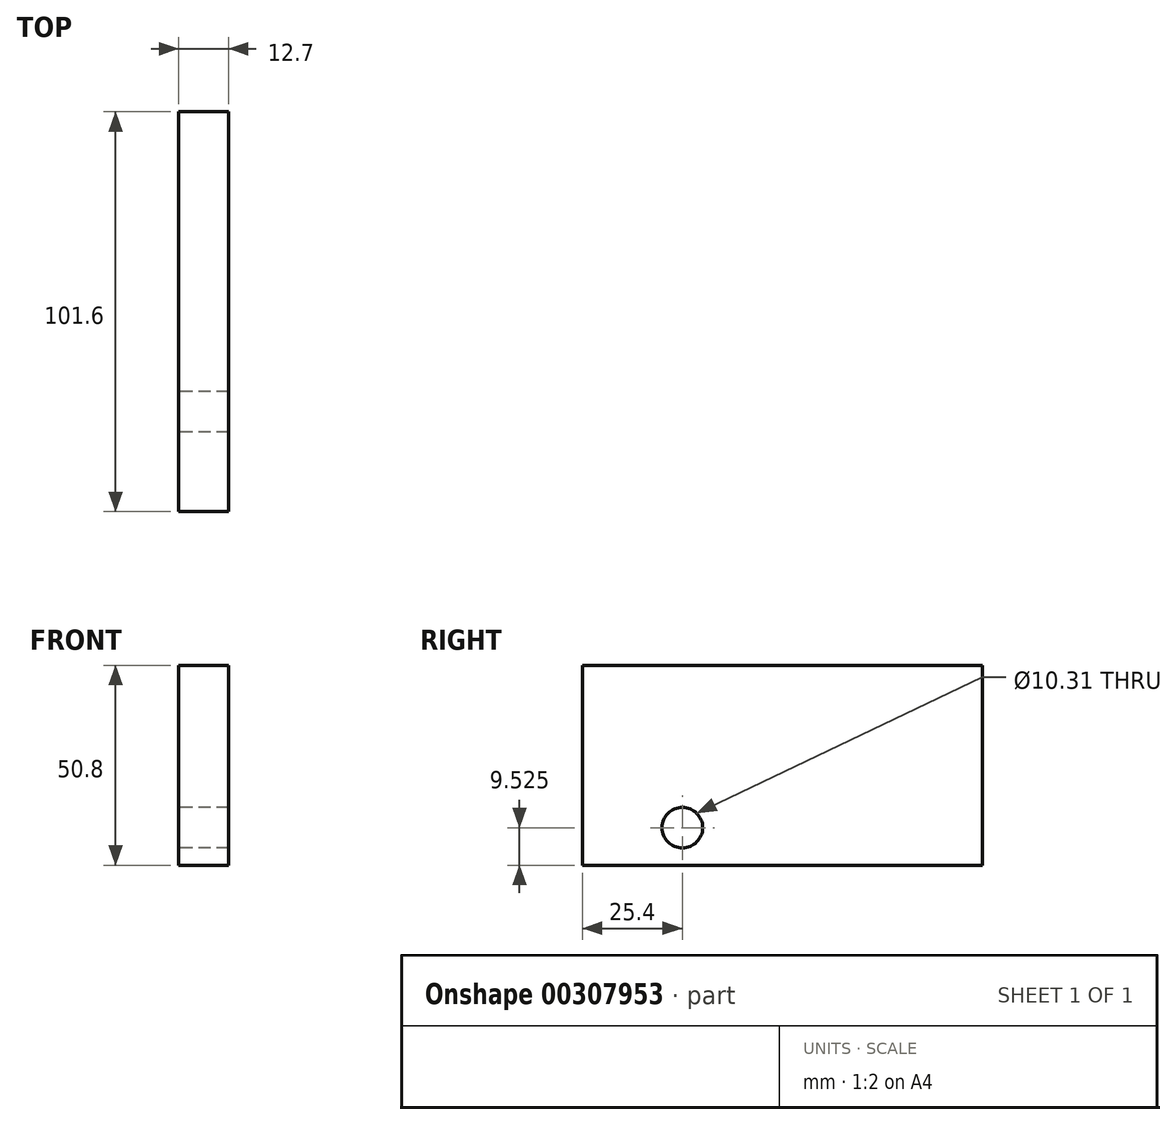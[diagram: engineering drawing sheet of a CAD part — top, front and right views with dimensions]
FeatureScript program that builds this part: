
annotation { "Feature Type Name" : "Feature", "Feature Type Description" : "" }
export const myFeature = defineFeature(function(context is Context, id is Id, definition is map)
    precondition{}
    {
        {
            var Q0;
            Q0=qCreatedBy(makeId("Right.planeOp"),FACE);
            var sketch = newSketch(context, id + "F0", { "sketchPlane" : qUnion([Q0])});
            skLineSegment(sketch, "E0.bottom", {"start": v(-50.8, 25.4) * mm, "end": v(50.8, 25.4) * mm});
            skLineSegment(sketch, "E0.top", {"start": v(-50.8, -25.4) * mm, "end": v(50.8, -25.4) * mm});
            skLineSegment(sketch, "E0.left", {"start": v(-50.8, 25.4) * mm, "end": v(-50.8, -25.4) * mm});
            skLineSegment(sketch, "E0.right", {"start": v(50.8, 25.4) * mm, "end": v(50.8, -25.4) * mm});
            skPoint(sketch, "E0.middle", {"position": v(0, 0) * mm});
            skCircle(sketch, "E1", {"center": v(-25.4, -15.88) * mm, "radius": 5.16 * mm});
            skSolve(sketch);
        }
        {
            var Q0;
            Q0=makeQuery(id+"F0.imprint","IMPRINT",FACE,{"disambiguationData":[TD([[makeQuery(id+"F0.imprint","IMPRINT",EDGE,{"derivedFrom":sQuery(id+"F0.wireOp",EDGE,"E0.bottom")}),-1.0]])]});
            extrude(context, id + "F1", {"entities" : qUnion([Q0]), "endBound" : BoundingType.SYMMETRIC, "depth" : 12.7 * mm});
        }
    });
